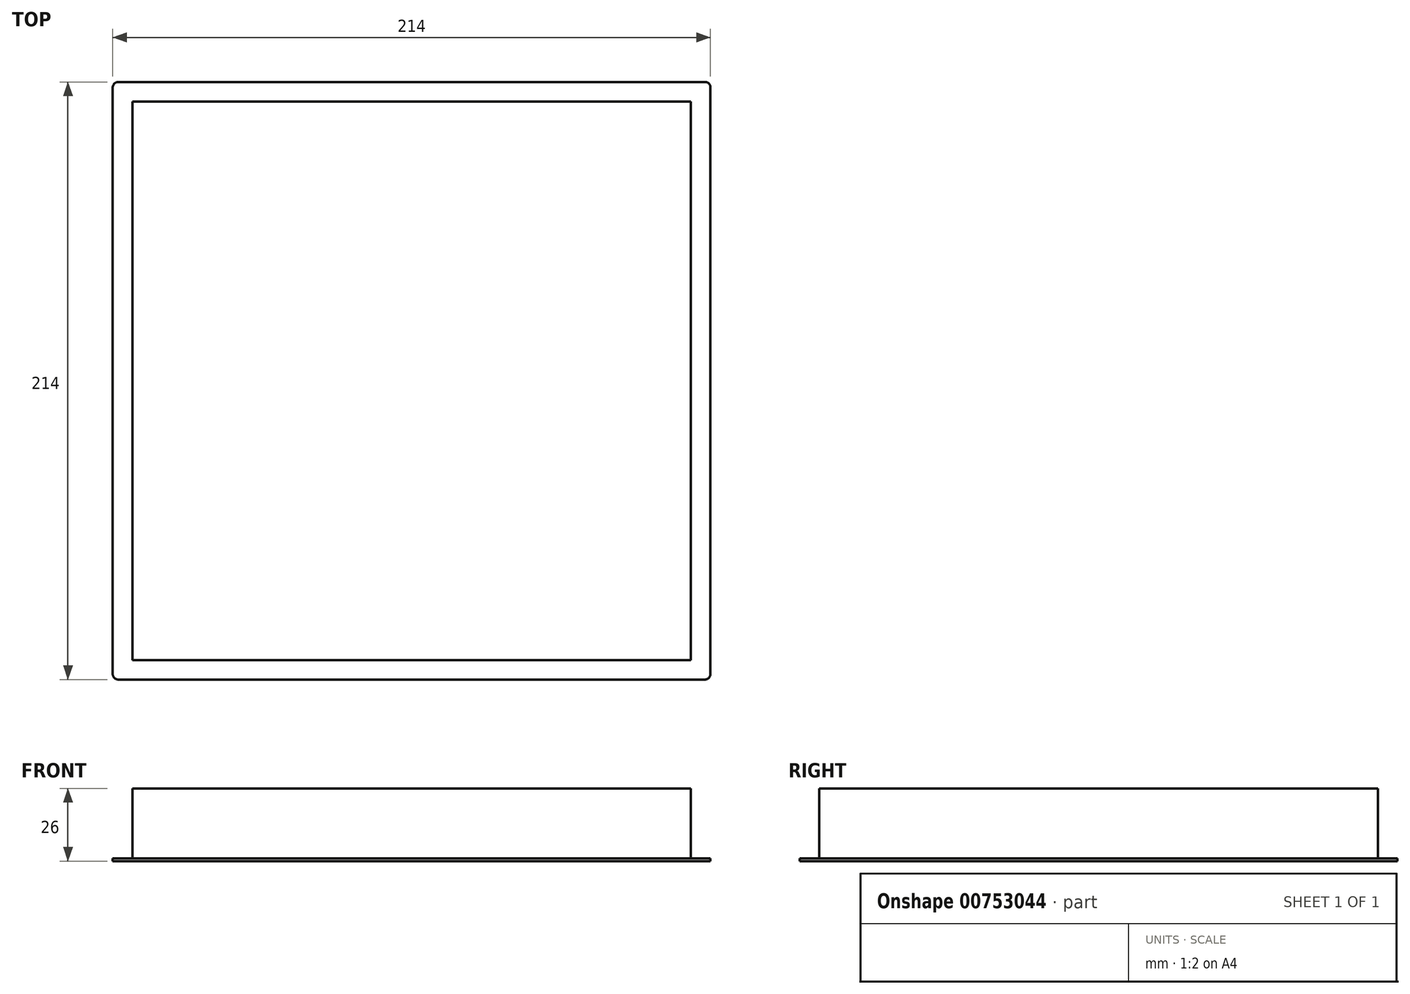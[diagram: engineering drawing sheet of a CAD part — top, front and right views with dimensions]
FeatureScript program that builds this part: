
annotation { "Feature Type Name" : "Feature", "Feature Type Description" : "" }
export const myFeature = defineFeature(function(context is Context, id is Id, definition is map)
    precondition{}
    {
        {
            var Q0;
            Q0=qCreatedBy(makeId("Top.planeOp"),FACE);
            var sketch = newSketch(context, id + "F0", { "sketchPlane" : qUnion([Q0])});
            skLineSegment(sketch, "E0.bottom", {"start": v(-107, 107) * mm, "end": v(107, 107) * mm});
            skLineSegment(sketch, "E0.top", {"start": v(-107, -107) * mm, "end": v(107, -107) * mm});
            skLineSegment(sketch, "E0.left", {"start": v(-107, 107) * mm, "end": v(-107, -107) * mm});
            skLineSegment(sketch, "E0.right", {"start": v(107, 107) * mm, "end": v(107, -107) * mm});
            skSolve(sketch);
        }
        {
            var Q0;
            Q0=makeQuery(id+"F0.imprint","IMPRINT",FACE,{"disambiguationData":[TD([[makeQuery(id+"F0.imprint","IMPRINT",EDGE,{"derivedFrom":sQuery(id+"F0.wireOp",EDGE,"E0.bottom")}),-1.0]])]});
            extrude(context, id + "F1", {"entities" : qUnion([Q0]), "depth" : 1 * mm, "offsetDistance" : 25 * mm});
        }
        {
            var Q0;
            Q0=makeQuery(id+"F1.opExtrude","SWEPT_EDGE",EDGE,{"disambiguationData":[OSD([sQuery(id+"F0.wireOp",EDGE,"E0.top"),sQuery(id+"F0.wireOp",EDGE,"E0.left")])]});
            var Q1;
            Q1=makeQuery(id+"F1.opExtrude","SWEPT_EDGE",EDGE,{"disambiguationData":[OSD([sQuery(id+"F0.wireOp",EDGE,"E0.top"),sQuery(id+"F0.wireOp",EDGE,"E0.right")])]});
            var Q2;
            Q2=makeQuery(id+"F1.opExtrude","SWEPT_EDGE",EDGE,{"disambiguationData":[OSD([sQuery(id+"F0.wireOp",EDGE,"E0.bottom"),sQuery(id+"F0.wireOp",EDGE,"E0.right")])]});
            var Q3;
            Q3=makeQuery(id+"F1.opExtrude","SWEPT_EDGE",EDGE,{"disambiguationData":[OSD([sQuery(id+"F0.wireOp",EDGE,"E0.bottom"),sQuery(id+"F0.wireOp",EDGE,"E0.left")])]});
            fillet(context, id + "F2", {"entities" : qUnion([Q0, Q1, Q2, Q3]), "radius" : 2 * mm, "tangentPropagation" : true, "allowEdgeOverflow" : false});
        }
        {
            var Q0;
            Q0=makeQuery(id+"F1.opExtrude","CAP_FACE",FACE,{"disambiguationData":[OSD([sQuery(id+"F0.wireOp",EDGE,"E0.bottom"),sQuery(id+"F0.wireOp",EDGE,"E0.top"),sQuery(id+"F0.wireOp",EDGE,"E0.left"),sQuery(id+"F0.wireOp",EDGE,"E0.right")])],"isStart":false});
            var sketch = newSketch(context, id + "F3", { "sketchPlane" : qUnion([Q0])});
            skLineSegment(sketch, "E1.bottom", {"start": v(-100, 100) * mm, "end": v(100, 100) * mm});
            skLineSegment(sketch, "E1.top", {"start": v(-100, -100) * mm, "end": v(100, -100) * mm});
            skLineSegment(sketch, "E1.left", {"start": v(-100, 100) * mm, "end": v(-100, -100) * mm});
            skLineSegment(sketch, "E1.right", {"start": v(100, 100) * mm, "end": v(100, -100) * mm});
            skSolve(sketch);
        }
        {
            var Q0;
            Q0=makeQuery(id+"F3.imprint","IMPRINT",FACE,{"disambiguationData":[TD([[makeQuery(id+"F3.imprint","IMPRINT",EDGE,{"derivedFrom":sQuery(id+"F3.wireOp",EDGE,"E1.bottom")}),-1.0]])]});
            extrude(context, id + "F4", {"entities" : qUnion([Q0]), "depth" : 25 * mm, "offsetDistance" : 25 * mm});
        }
    });
